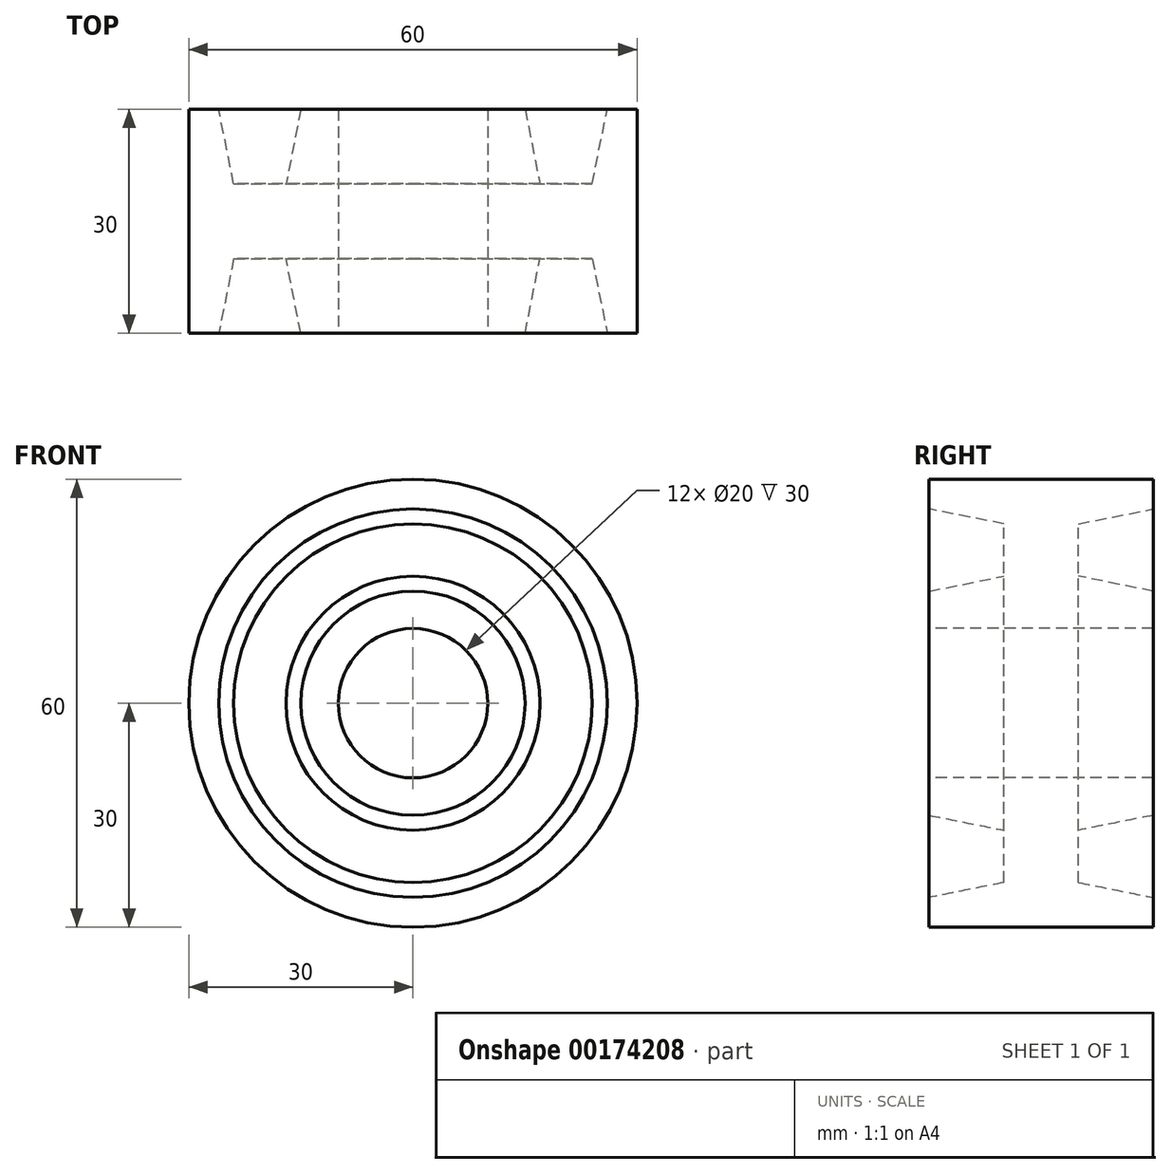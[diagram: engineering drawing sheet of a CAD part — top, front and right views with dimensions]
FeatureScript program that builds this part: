
annotation { "Feature Type Name" : "Feature", "Feature Type Description" : "" }
export const myFeature = defineFeature(function(context is Context, id is Id, definition is map)
    precondition{}
    {
        {
            var Q0;
            Q0=qCreatedBy(makeId("Right.planeOp"),FACE);
            var sketch = newSketch(context, id + "F0", { "sketchPlane" : qUnion([Q0])});
            skLineSegment(sketch, "E0", {"start": v(-15, 0) * mm, "end": v(15, 0) * mm, "construction": true});
            skLineSegment(sketch, "E1", {"start": v(0, 0) * mm, "end": v(0, -30) * mm, "construction": true});
            skLineSegment(sketch, "E2", {"start": v(15, -30) * mm, "end": v(-15, -30) * mm});
            skLineSegment(sketch, "E3", {"start": v(15, -30) * mm, "end": v(15, -26) * mm});
            skLineSegment(sketch, "E4", {"start": v(15, -26) * mm, "end": v(5, -24) * mm});
            skLineSegment(sketch, "E5", {"start": v(5, -24) * mm, "end": v(5, -17) * mm});
            skLineSegment(sketch, "E6", {"start": v(5, -17) * mm, "end": v(15, -15) * mm});
            skLineSegment(sketch, "E7", {"start": v(15, -15) * mm, "end": v(15, -10) * mm});
            skLineSegment(sketch, "E8", {"start": v(15, -10) * mm, "end": v(0, -10) * mm});
            skLineSegment(sketch, "E9", {"start": v(5, -20.5) * mm, "end": v(18.53, -20.5) * mm, "construction": true});
            skLineSegment(sketch, "E10.MirrorCS", {"start": v(-15, -30) * mm, "end": v(-15, -26) * mm});
            skLineSegment(sketch, "E11.MirrorCS", {"start": v(-15, -26) * mm, "end": v(-5, -24) * mm});
            skLineSegment(sketch, "E12.MirrorCS", {"start": v(-5, -24) * mm, "end": v(-5, -17) * mm});
            skLineSegment(sketch, "E13.MirrorCS", {"start": v(-5, -17) * mm, "end": v(-15, -15) * mm});
            skLineSegment(sketch, "E14.MirrorCS", {"start": v(-15, -10) * mm, "end": v(0, -10) * mm});
            skLineSegment(sketch, "E15.MirrorCS", {"start": v(-15, -15) * mm, "end": v(-15, -10) * mm});
            skSolve(sketch);
        }
        {
            var Q0;
            Q0 = qSketchRegion(id + "F0", true);
            var Q1;
            Q1=sQuery(id+"F0.wireOp",EDGE,"E0");
            revolve(context, id + "F1", {"entities" : qUnion([Q0]), "axis" : qUnion([Q1]), "revolveType" : RevolveType.FULL});
        }
    });
